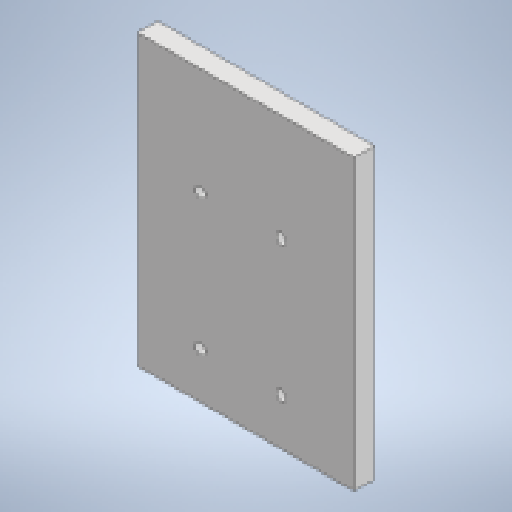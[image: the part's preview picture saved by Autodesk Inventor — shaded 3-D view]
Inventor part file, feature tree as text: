
AUTODESK INVENTOR PART (.ipt)
format: ipt  version: 2025.1 (Build 291241000, 241)  size: 616,960 bytes
history: native  units: mm
features: fillet x9, extrude x7, sketch x6, other x5, reference x5, projected_geometry x2
ambient origin geometry x8: Origin, YZ Plane, XZ Plane, XY Plane, X Axis, Y Axis, Z Axis, Center Point
bodies: Body1 (feature_tree)
feature tree (34):
  other  "ソリッド1"
  extrude  "押し出し1"  Depth=2.5mm
  extrude  "押し出し2"  Depth=2.5mm
  extrude  "押し出し3"  Depth=2.5mm
  sketch  "スケッチ4"
  extrude  "押し出し4"  Depth=2.5mm
  extrude  "押し出し5"  Depth=5.0mm
  fillet  "フィレット1"  Radius=10.0mm
  extrude  "押し出し7"  Depth=5.0mm TaperAngle=0.0deg
  fillet  "フィレット10"  Radius=95.0mm
  fillet  "フィレット11"  Radius=60.0mm
  fillet  "フィレット12"  Radius=2.2mm
  fillet  "フィレット13"  Radius=2.2mm
  extrude  "押し出し8"  Depth=2.2mm
  fillet  "フィレット14"  Radius=2.2mm
  fillet  "フィレット15"  [1 undecoded]
  fillet  "フィレット16"  Radius=4.0mm
  fillet  "フィレット17"  Radius=4.0mm
  sketch  "スケッチ1"
  reference  "参照1"
  reference  "参照2"
  reference  "参照3"
  reference  "参照4"
  reference  "参照5"
  sketch  "スケッチ2"
  projected_geometry  "投影ループ1"
  sketch  "スケッチ3"
  sketch  "スケッチ6"
  projected_geometry  "投影ループ3"
  sketch  "スケッチ7"
  other  "<userpath>\Documents\Inventor\Vixen\doutai.iam"
  other  "doutai.iam"
  other  "asikubi_asi:2"
  other  "asikubi_asi:1"
note: 1 required parameter value undecoded (feature->parameter linkage not recoverable at this tier; creation-order binding heuristic only, values carry confidence <= 0.55)
